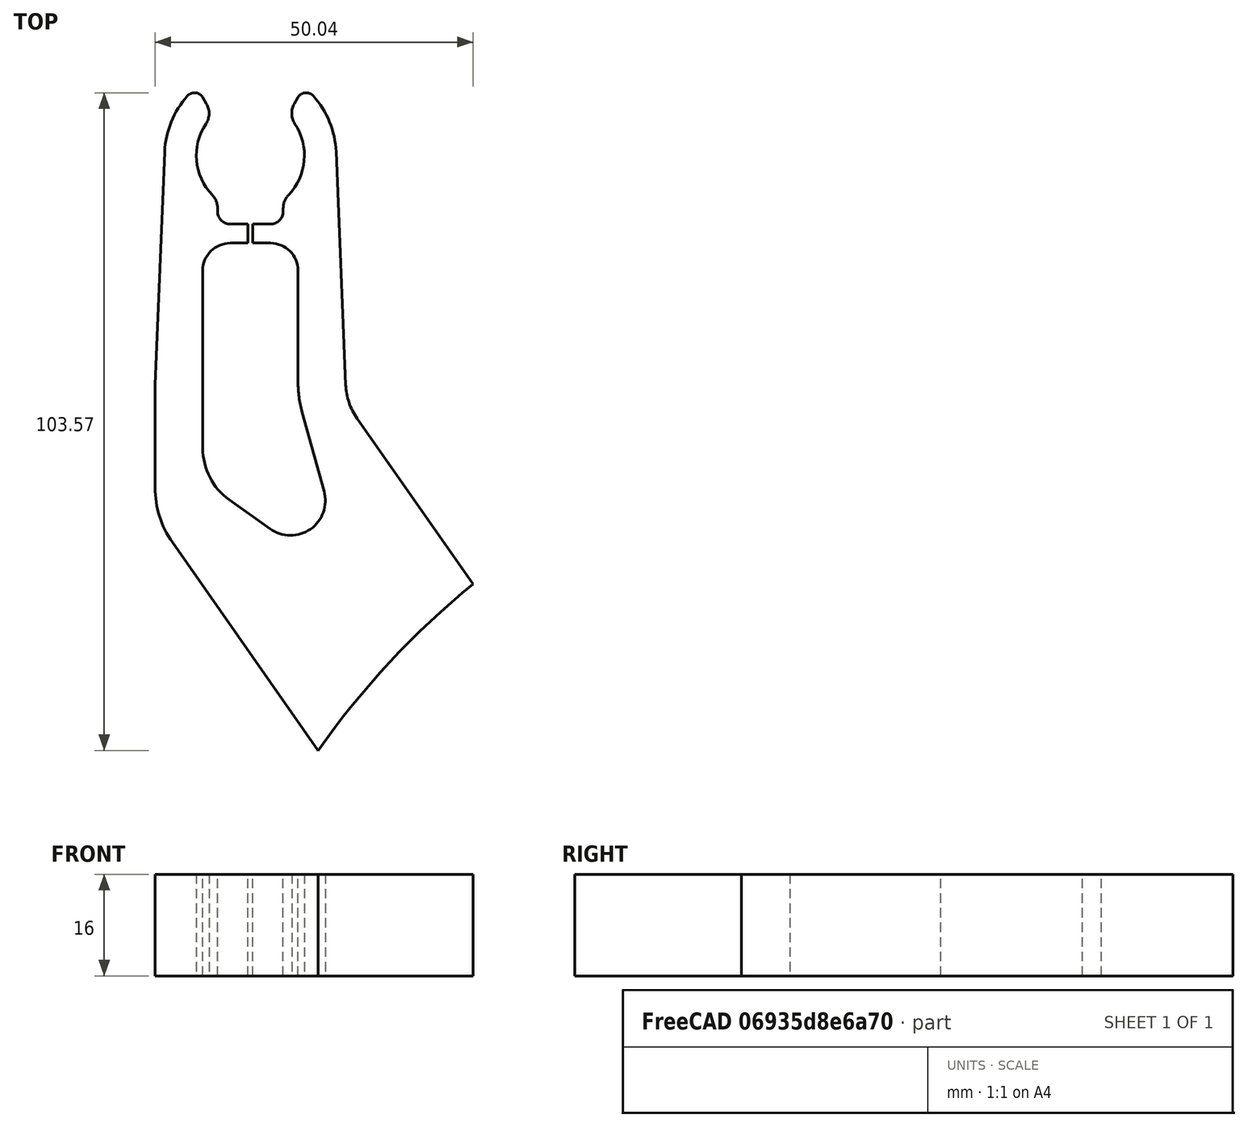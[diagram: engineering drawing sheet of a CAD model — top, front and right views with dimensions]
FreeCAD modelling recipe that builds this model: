
FCSTD DOCUMENT  (FreeCAD 0.19R20655 (Git))
Label: Clamp
License: All rights reserved
LicenseURL: http://en.wikipedia.org/wiki/All_rights_reserved
objects: Spreadsheet::Sheet×1, Sketcher::SketchObject×1, PartDesign::Pad×1, PartDesign::Body×1, Raytracing::RayFeature×1, Raytracing::RayProject×1
note: 4 computed .brp shape members not serialized (recipe doc carries the construction recipe); baked Part::Feature solids carry a one-line shape summary decoded from their .brp

FEATURE [Spreadsheet::Sheet] Spreadsheet
  cells = A1=spark gap; B1(spark_gap)=15; A2=stage rotation; B2(stage_rotation)==asin((spark_gap + ball_steel_D) / (2 * stage_center_offset)); C2=Rotation of left stages column in negative direction and righ column in positive direction; A3=stage center offset; B3(stage_center_offset)==hv_clamp_h_tot + pole_clamp_R; C3=Offset of capacitor stage center of rotation from pole vertical center; A4=stage length; B4(stage_length)==murata_l + 2 * tube_l + ball_steel_D; A6=ball_steel D; B6(ball_steel_D)=70; A8=tube D; B8(tube_D)=18; A9=tube d; B9(tube_d)=15; A10=tube l; B10(tube_l)=20; A12=Murata D; B12(murata_D)=60; A13=Murata l; B13(murata_l)=32; A15=res_100k D; B15(res_100k_D)=11; A16=res_100k l; B16(res_100k_l)=147; A18=KG D; B18(KG_D)=250; A19=KG d; B19(KG_d)==250 - 2 * 7.7; A20=KG l; B20(KG_l)=1000; A22=pole clamp l; B22(pole_clamp_l)=120; A23=pole clamp degrees; B23(pole_clamp_degrees)=90; A24=pole clamp R; B24(pole_clamp_R)==KG_D / 2 + (KG_D - KG_d) / 2; A26=HV_Clamp l; B26(hv_clamp_l)=16; A27=HV_Clamp h; B27(hv_clamp_h)=30; A28=HV_Clamp w; B28(hv_clamp_w)=30; A29=HV_Clamp h_tot; B29(hv_clamp_h_tot)=75; A30=HV_clamp_filllet_inner; B30(hv_clamp_fillet_inner)=3; A31=HV_clamp_fillet_outer; B31(hv_clamp_fillet_outer)=1.5; A32=HV_clamp_gap; B32(hv_clamp_gap)==14 - 2 * hv_clamp_pretensioning; A33=HV_clamp_pretensioning; B33(hv_clamp_pretensioning)=0.5
FEATURE [Sketcher::SketchObject] Sketch008
  MapMode = 5
  Support = -> [XY_Plane]
  expr: Constraints[1] = Spreadsheet.hv_clamp_w
  expr: Constraints[12] = Spreadsheet.pole_clamp_R
  expr: Constraints[40] = Spreadsheet.hv_clamp_fillet_outer
  expr: Constraints[11] = Spreadsheet.hv_clamp_h_tot
  expr: Constraints[117] = Spreadsheet.hv_clamp_pretensioning
  expr: Constraints[101] = Spreadsheet.tube_D / 2
  expr: Constraints[37] = Spreadsheet.hv_clamp_fillet_outer
  expr: Constraints[32] = Spreadsheet.hv_clamp_fillet_inner
  expr: Constraints[48] = Spreadsheet.hv_clamp_gap + 2 * Spreadsheet.hv_clamp_fillet_inner
  expr: Constraints[44] = 3
  expr: Constraints[17] = Spreadsheet.hv_clamp_w + 5
  sketch-geometry (48):
    g0: LineSegment [constr] StartX=15 StartY=-36.1034 StartZ=0 EndX=-15 EndY=-36.1034 EndZ=0
    g1: LineSegment StartX=-15 StartY=-36.1034 StartZ=0 EndX=-13.4881 EndY=0.576563 EndZ=0
    g2: LineSegment StartX=15 StartY=-36.1034 StartZ=0 EndX=13.4881 EndY=0.576563 EndZ=0
    g3: LineSegment StartX=-7.47684 StartY=9.12903 StartZ=0 EndX=-6.90192 EndY=8.13325 EndZ=0
    g4: LineSegment StartX=7.47684 StartY=9.12903 StartZ=0 EndX=6.90192 EndY=8.13325 EndZ=0
    g5: ArcOfCircle CenterX=-0.5 CenterY=0 CenterZ=0 NormalX=0 NormalY=0 NormalZ=1 AngleXU=0 Radius=14 StartAngle=0.0411947 EndAngle=0.734643
    g6: ArcOfCircle CenterX=0.5 CenterY=0 CenterZ=0 NormalX=0 NormalY=0 NormalZ=1 AngleXU=0 Radius=9 StartAngle=2.55591 EndAngle=3.90538
    g7: ArcOfCircle CenterX=0.5 CenterY=0 CenterZ=0 NormalX=0 NormalY=0 NormalZ=1 AngleXU=0 Radius=14 StartAngle=2.40695 EndAngle=3.1004
    g8: LineSegment [constr] StartX=-15 StartY=-36.1034 StartZ=0 EndX=15 EndY=-36.1034 EndZ=0
    g9: LineSegment StartX=10.6664 StartY=-93.6883 StartZ=0 EndX=-12.2873 EndY=-60.9071 EndZ=0
    g10: LineSegment StartX=-15 StartY=-36.1034 StartZ=0 EndX=-15 EndY=-52.3034 EndZ=0
    g11: ArcOfCircle CenterX=119.132 CenterY=-170.138 CenterZ=0 NormalX=0 NormalY=0 NormalZ=1 AngleXU=0 Radius=132.7 StartAngle=2.25709 EndAngle=2.52763
    g12: LineSegment [constr] StartX=0 StartY=0 StartZ=0 EndX=43.0182 EndY=-61.4364 EndZ=0
    g13: LineSegment [constr] StartX=43.0182 StartY=-61.4364 StartZ=0 EndX=119.132 EndY=-170.138 EndZ=0
    g14: LineSegment StartX=35.0431 StartY=-67.4813 StartZ=0 EndX=16.8 EndY=-41.4273 EndZ=0
    g15: Circle [constr] CenterX=119.132 CenterY=-170.138 CenterZ=0 NormalX=0 NormalY=0 NormalZ=1 AngleXU=0 Radius=132.7
    g16: ArcOfCircle CenterX=-0.5 CenterY=0 CenterZ=0 NormalX=0 NormalY=0 NormalZ=1 AngleXU=0 Radius=9 StartAngle=5.5194 EndAngle=6.86887
    g17: LineSegment StartX=-7.5 StartY=-18.1333 StartZ=0 EndX=-7.5 EndY=-46.09 EndZ=0
    g18: LineSegment StartX=7.5 StartY=-35.6916 StartZ=0 EndX=7.5 EndY=-18.1333 EndZ=0
    g19: LineSegment StartX=-3.30796 StartY=-54.2305 StartZ=0 EndX=3.10866 EndY=-58.8086 EndZ=0
    g20: LineSegment StartX=8.13669 StartY=-40.3679 StartZ=0 EndX=11.6028 EndY=-52.8609 EndZ=0
    g21: ArcOfCircle CenterX=6.30304 CenterY=-54.3313 CenterZ=0 NormalX=0 NormalY=0 NormalZ=1 AngleXU=0 Radius=5.5 StartAngle=4.09268 EndAngle=6.55383
    g22: LineSegment [constr] StartX=35.0431 StartY=-67.4813 StartZ=0 EndX=10.6664 EndY=-93.6883 EndZ=0
    g23: ArcOfCircle CenterX=-9.5 CenterY=6.63325 CenterZ=0 NormalX=0 NormalY=0 NormalZ=1 AngleXU=0 Radius=3 StartAngle=5.6975 EndAngle=6.80678
    g24: ArcOfCircle CenterX=9.5 CenterY=6.63325 CenterZ=0 NormalX=0 NormalY=0 NormalZ=1 AngleXU=0 Radius=3 StartAngle=2.61799 EndAngle=3.72728
    g25: ArcOfCircle CenterX=8.77588 CenterY=8.37903 CenterZ=0 NormalX=0 NormalY=0 NormalZ=1 AngleXU=0 Radius=1.5 StartAngle=0.734643 EndAngle=2.61799
    g26: ArcOfCircle CenterX=-8.77588 CenterY=8.37903 CenterZ=0 NormalX=0 NormalY=0 NormalZ=1 AngleXU=0 Radius=1.5 StartAngle=0.523599 EndAngle=2.40695
    g27: LineSegment StartX=-0.4 StartY=-10.7999 StartZ=0 EndX=-0.4 EndY=-13.7999 EndZ=0
    g28: LineSegment StartX=0.4 StartY=-10.7999 StartZ=0 EndX=0.4 EndY=-13.7999 EndZ=0
    g29: LineSegment StartX=-3.16667 StartY=-13.7999 StartZ=0 EndX=-0.4 EndY=-13.7999 EndZ=0
    g30: LineSegment StartX=0.4 StartY=-13.7999 StartZ=0 EndX=3.16667 EndY=-13.7999 EndZ=0
    g31: ArcOfCircle CenterX=2.5 CenterY=-46.09 CenterZ=0 NormalX=0 NormalY=0 NormalZ=1 AngleXU=0 Radius=10 StartAngle=3.14159 EndAngle=4.09268
    g32: ArcOfCircle CenterX=24.9915 CenterY=-35.6916 CenterZ=0 NormalX=0 NormalY=0 NormalZ=1 AngleXU=0 Radius=17.4915 StartAngle=3.14159 EndAngle=3.41223
    g33: ArcOfCircle CenterX=1e-15 CenterY=-52.3034 CenterZ=0 NormalX=0 NormalY=0 NormalZ=1 AngleXU=0 Radius=15 StartAngle=3.14159 EndAngle=3.75246
    g34: ArcOfCircle CenterX=24.9915 CenterY=-35.6916 CenterZ=0 NormalX=0 NormalY=0 NormalZ=1 AngleXU=0 Radius=10 StartAngle=3.18279 EndAngle=3.75246
    g35: ArcOfCircle CenterX=-3.16667 CenterY=-18.1333 CenterZ=0 NormalX=0 NormalY=0 NormalZ=1 AngleXU=0 Radius=4.33333 StartAngle=1.5708 EndAngle=3.14159
    g36: ArcOfCircle CenterX=3.16667 CenterY=-18.1333 CenterZ=0 NormalX=0 NormalY=0 NormalZ=1 AngleXU=0 Radius=4.33333 StartAngle=3e-16 EndAngle=1.5708
    g37: LineSegment StartX=0.4 StartY=-10.7999 StartZ=0 EndX=3.16667 EndY=-10.7999 EndZ=0
    g38: LineSegment StartX=-3.16667 StartY=-10.7999 StartZ=0 EndX=-0.4 EndY=-10.7999 EndZ=0
    g39: ArcOfCircle CenterX=-8.16667 CenterY=-8.29993 CenterZ=0 NormalX=0 NormalY=0 NormalZ=1 AngleXU=0 Radius=3 StartAngle=3e-16 EndAngle=0.763786
    g40: ArcOfCircle CenterX=-3.16667 CenterY=-8.79993 CenterZ=0 NormalX=0 NormalY=0 NormalZ=1 AngleXU=0 Radius=2 StartAngle=3.14159 EndAngle=4.71239
    g41: LineSegment StartX=-5.16667 StartY=-8.29993 StartZ=0 EndX=-5.16667 EndY=-8.79993 EndZ=0
    g42: ArcOfCircle CenterX=8.16667 CenterY=-8.29993 CenterZ=0 NormalX=0 NormalY=0 NormalZ=1 AngleXU=0 Radius=3 StartAngle=2.37781 EndAngle=3.14159
    g43: LineSegment StartX=5.16667 StartY=-8.29993 StartZ=0 EndX=5.16667 EndY=-8.79993 EndZ=0
    g44: ArcOfCircle CenterX=3.16667 CenterY=-8.79993 CenterZ=0 NormalX=0 NormalY=0 NormalZ=1 AngleXU=0 Radius=2 StartAngle=4.71239 EndAngle=6.28319
    g45: LineSegment [constr] StartX=0 StartY=0 StartZ=0 EndX=0.5 EndY=0 EndZ=0
    g46: LineSegment [constr] StartX=0 StartY=0 StartZ=0 EndX=-0.5 EndY=0 EndZ=0
    g47: LineSegment [constr] StartX=6.30304 StartY=-54.3313 StartZ=0 EndX=24.5462 EndY=-80.3852 EndZ=0
  constraints (119):
    c: Horizontal(g0)
    c: Distance(g0) = 30
    c: Coincident(g1,g0)
    c: Coincident(g2,g0)
    c: Angle(g3) = -1.0472
    c: Angle(g4) = -2.0944
    c: Coincident(g5,g2)
    c: Coincident(g0,g8)
    c: Coincident(g10,g8)
    c: Coincident(g8,g0)
    c: Coincident(g13,g12)
    c: Distance(g12) = 75
    c: Distance(g13) = 132.7
    c: Coincident(g11,g13)
    c: Coincident(g11,g9)
    c: Parallel(g9,g14)
    c: Vertical(g10)
    c: Distance(g14,g9) = 35
    c: Coincident(g11,g14)
    c: Coincident(g15,g11)
    c: PointOnObject(g9,g15)
    c: Perpendicular(g15,g12)
    c: Parallel(g14,g12)
    c: PointOnObject(g12,g15)
    c: Vertical(g17)
    c: Vertical(g18)
    c: Distance(g21,g9) = 19
    c: Coincident(g22,g11)
    c: Coincident(g22,g9)
    c: Distance(g21,g22) = 30
    c: Tangent(g3,g23) = 1.5708
    c: Tangent(g23,g6) = 1.5708
    c: Radius(g23) = 3
    c: Tangent(g24,g4) = -1.5708
    c: Tangent(g16,g24) = 1.5708
    c: Tangent(g25,g4) = -1.5708
    c: Tangent(g25,g5) = -1.5708
    c: Radius(g25) = 1.5
    c: Tangent(g26,g7) = -1.5708
    c: Tangent(g26,g3) = 1.5708
    c: Radius(g26) = 1.5
    c: Symmetric(g23,g24,g-2)
    c: Symmetric(g17,g18,g-2)
    c: Vertical(g27)
    c: Distance(g27) = 3
    c: Coincident(g29,g27)
    c: Coincident(g30,g28)
    c: Symmetric(g27,g28,g-2)
    c: DistanceX(g23,g24) = 19
    c: Tangent(g21,g20) = 1.5708
    c: Tangent(g31,g17) = -1.5708
    c: Tangent(g19,g31) = -1.5708
    c: Tangent(g32,g18) = 1.5708
    c: Tangent(g32,g20) = -1.5708
    c: Tangent(g21,g19) = -1.5708
    c: Radius(g21) = 5.5
    c: Tangent(g33,g9) = 1.5708
    c: Tangent(g33,g10) = -1.5708
    c: Tangent(g34,g2) = 1.5708
    c: Tangent(g14,g34) = 1.5708
    c: Radius(g34) = 10
    c: Coincident(g32,g34)
    c: Radius(g31) = 10
    c: Radius(g33) = 15
    c: Tangent(g35,g29) = 1.5708
    c: Tangent(g35,g17) = -1.5708
    c: Tangent(g36,g30) = 1.5708
    c: Tangent(g36,g18) = -1.5708
    c: Equal(g36,g35)
    c: Horizontal(g30)
    c: Symmetric(g6,g16,g-2)
    c: Vertical(g28)
    c: Horizontal(g37)
    c: Equal(g30,g37)
    c: Coincident(g37,g28)
    c: Horizontal(g38)
    c: Equal(g38,g30)
    c: Coincident(g38,g27)
    c: Tangent(g39,g6) = 1.5708
    c: Tangent(g40,g38) = -1.5708
    c: Radius(g40) = 2
    c: Vertical(g41)
    c: Tangent(g41,g40) = -1.5708
    c: Tangent(g39,g41) = 1.5708
    c: Equal(g39,g42)
    c: Tangent(g42,g16) = 1.5708
    c: Vertical(g43)
    c: Tangent(g43,g42) = -1.5708
    c: Tangent(g44,g43) = 1.5708
    c: Tangent(g44,g37) = -1.5708
    c: Equal(g27,g28)
    c: DistanceX(g6,g16) = 12
    c: DistanceX(g27,g28) = 0.8
    c: Distance(g41) = 0.5
    c: Radius(g39) = 3
    c: Distance(g1,g17) = 7.5
    c: Distance(g2,g18) = 7.5
    c: Angle(g14) = 2.18166
    c: Coincident(g7,g6)
    c: Coincident(g45,g-1)
    c: Coincident(g46,g45)
    c: Radius(g6) = 9
    c: Coincident(g12,g-1)
    c: Coincident(g5,g16)
    c: Coincident(g5,g46)
    c: Coincident(g6,g45)
    c: Equal(g5,g7)
    c: Equal(g1,g2)
    c: Coincident(g47,g21)
    c: Equal(g47,g14)
    c: Symmetric(g19,g20,g47)
    c: Parallel(g47,g9)
    c: Tangent(g1,g7) = 1.5708
    c: Distance(g14,g12) = 10
    c: Horizontal(g46)
    c: Horizontal(g45)
    c: Equal(g46,g45)
    c: Distance(g46) = 0.5
    c: Radius(g7) = 14
FEATURE [PartDesign::Pad] Pad
  AllowMultiFace = false
  Length = 16
  Length2 = 100
  Profile = -> Sketch008
  Refine = true
  Type = 0
  expr: Length = Spreadsheet.hv_clamp_l
FEATURE [PartDesign::Body] Body
  Group = -> [Sketch008,Pad]
  Origin = -> Origin
  Tip = -> Pad
FEATURE [Raytracing::RayFeature] Body_View
  Result = <blob: 47349 chars omitted>
  Source = -> Body
  Transparency = 0
FEATURE [Raytracing::RayProject] PovProject
  Camera = // declares position and view direction\n\n// Generated by FreeCAD (http://www.freecadweb.org/)\n#declare cam_location =  <11.2448,171.117,-120.311>;\n#declare cam_look_at  = <11.8598,-4.11116,-42.0082>;\n#declare cam_sky      = <0.573609,0.335865,0.747106>;\n#declare cam_angle    = 45; \ncamera {\n  location  cam_location\n  look_at   cam_look_at\n  sky       cam_sky\n  angle     cam_angle \n  right x*1920/1080\n}
  Group = -> [Body_View]
  Template = <path>
note: 1 file-system path scrubbed to <path> (originals preserved in the JSON sidecar)
